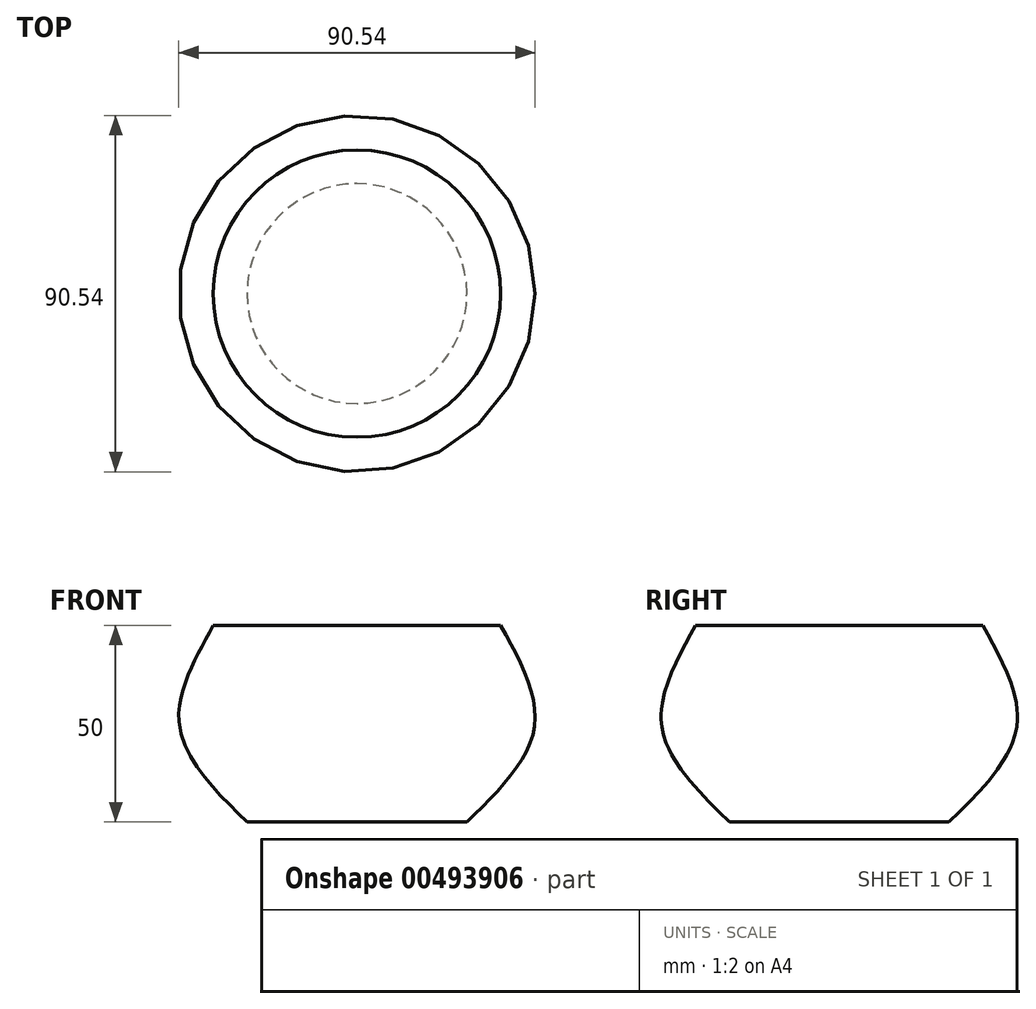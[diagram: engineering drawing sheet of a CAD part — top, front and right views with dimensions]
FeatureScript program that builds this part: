
annotation { "Feature Type Name" : "Feature", "Feature Type Description" : "" }
export const myFeature = defineFeature(function(context is Context, id is Id, definition is map)
    precondition{}
    {
        {
            var Q0;
            Q0=qCreatedBy(makeId("Top.planeOp"),FACE);
            cPlane(context, id + "F0", {"entities" : qUnion([Q0]), "cplaneType" : CPlaneType.OFFSET, "offset" : 25 * mm, "width" : 150 * mm, "height" : 150 * mm});
        }
        {
            var Q0;
            Q0=qCreatedBy(id+"F0.planeOp",FACE);
            cPlane(context, id + "F1", {"entities" : qUnion([Q0]), "cplaneType" : CPlaneType.OFFSET, "offset" : 25 * mm, "width" : 150 * mm, "height" : 150 * mm});
        }
        {
            var Q0;
            Q0=qCreatedBy(makeId("Top.planeOp"),FACE);
            var sketch = newSketch(context, id + "F2", { "sketchPlane" : qUnion([Q0])});
            skCircle(sketch, "E0", {"center": v(0, 0) * mm, "radius": 27.92 * mm});
            skSolve(sketch);
        }
        {
            var Q0;
            Q0=qCreatedBy(id+"F0.planeOp",FACE);
            var sketch = newSketch(context, id + "F3", { "sketchPlane" : qUnion([Q0])});
            skCircle(sketch, "E1", {"center": v(0, 0) * mm, "radius": 45.18 * mm});
            skSolve(sketch);
        }
        {
            var Q0;
            Q0=qCreatedBy(id+"F1.planeOp",FACE);
            var sketch = newSketch(context, id + "F4", { "sketchPlane" : qUnion([Q0])});
            skCircle(sketch, "E2", {"center": v(0, 0) * mm, "radius": 36.49 * mm});
            skSolve(sketch);
        }
        {
            var Q0;
            Q0=makeQuery(id+"F2.imprint","IMPRINT",FACE,{"disambiguationData":[TD([[makeQuery(id+"F2.imprint","IMPRINT",EDGE,{"derivedFrom":sQuery(id+"F2.wireOp",EDGE,"E0")}),1.0]])]});
            var Q1;
            Q1=makeQuery(id+"F3.imprint","IMPRINT",FACE,{"disambiguationData":[TD([[makeQuery(id+"F3.imprint","IMPRINT",EDGE,{"derivedFrom":sQuery(id+"F3.wireOp",EDGE,"E1")}),1.0]])]});
            var Q2;
            Q2=makeQuery(id+"F4.imprint","IMPRINT",FACE,{"disambiguationData":[TD([[makeQuery(id+"F4.imprint","IMPRINT",EDGE,{"derivedFrom":sQuery(id+"F4.wireOp",EDGE,"E2")}),1.0]])]});
            loft(context, id + "F5", {"sheetProfilesArray" : [{ "sheetProfileEntities" : qUnion([Q0]) }, { "sheetProfileEntities" : qUnion([Q1]) }, { "sheetProfileEntities" : qUnion([Q2]) }]});
        }
    });
